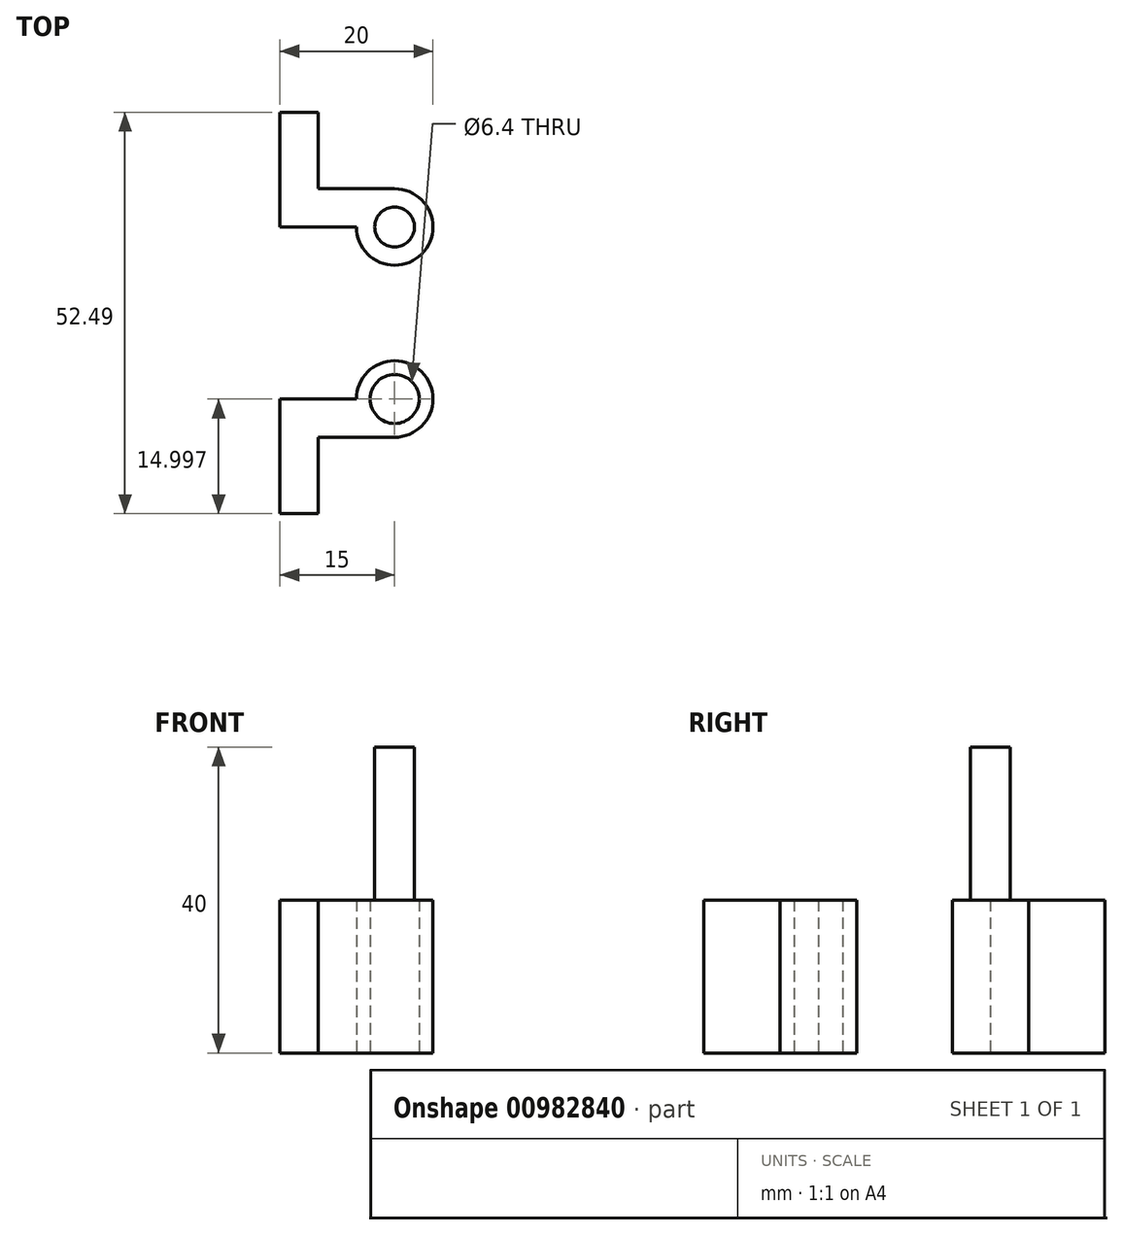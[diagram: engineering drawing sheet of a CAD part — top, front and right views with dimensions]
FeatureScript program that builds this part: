
annotation { "Feature Type Name" : "Feature", "Feature Type Description" : "" }
export const myFeature = defineFeature(function(context is Context, id is Id, definition is map)
    precondition{}
    {
        {
            var Q0;
            Q0=qCreatedBy(makeId("Top.planeOp"),FACE);
            var sketch = newSketch(context, id + "F0", { "sketchPlane" : qUnion([Q0])});
            skCircle(sketch, "E0", {"center": v(0, 0) * mm, "radius": 2.6 * mm});
            skLineSegment(sketch, "E1", {"start": v(-15, 5) * mm, "end": v(-15, 0) * mm});
            skLineSegment(sketch, "E2", {"start": v(-15, 0) * mm, "end": v(-5, 0) * mm});
            skCircle(sketch, "E3", {"center": v(0, -22.5) * mm, "radius": 3.2 * mm});
            skArc(sketch, "E4", {"start": v(0, -27.5) * mm, "mid": v(3.54, -18.96) * mm, "end": v(-5, -22.5) * mm});
            skLineSegment(sketch, "E5", {"start": v(-15, -22.5) * mm, "end": v(-15, -27.5) * mm});
            skLineSegment(sketch, "E6", {"start": v(-15, 5) * mm, "end": v(-15, 15) * mm});
            skLineSegment(sketch, "E7", {"start": v(-15, 15) * mm, "end": v(-10, 15) * mm});
            skLineSegment(sketch, "E8", {"start": v(-10, 15) * mm, "end": v(-10, 5) * mm});
            skLineSegment(sketch, "E9", {"start": v(-10, 5) * mm, "end": v(0, 5) * mm});
            skLineSegment(sketch, "E10", {"start": v(-15, -22.5) * mm, "end": v(-5, -22.5) * mm});
            skLineSegment(sketch, "E11", {"start": v(-15, -27.5) * mm, "end": v(-15, -37.5) * mm});
            skLineSegment(sketch, "E12", {"start": v(-15, -37.5) * mm, "end": v(-10, -37.5) * mm});
            skLineSegment(sketch, "E13", {"start": v(-10, -37.5) * mm, "end": v(-10, -27.5) * mm});
            skLineSegment(sketch, "E14", {"start": v(-10, -27.5) * mm, "end": v(0, -27.5) * mm});
            skArc(sketch, "E15", {"start": v(-5, 0) * mm, "mid": v(3.54, -3.54) * mm, "end": v(0, 5) * mm});
            skLineSegment(sketch, "E16", {"start": v(0, -2.6) * mm, "end": v(0, -5) * mm, "construction": true});
            skLineSegment(sketch, "E17", {"start": v(0, -27.5) * mm, "end": v(0, -25.7) * mm, "construction": true});
            skSolve(sketch);
        }
        {
            var Q0;
            Q0=makeQuery(id+"F0.imprint","IMPRINT",FACE,{"disambiguationData":[TD([[makeQuery(id+"F0.imprint","IMPRINT",EDGE,{"derivedFrom":sQuery(id+"F0.wireOp",EDGE,"E0")}),-1.0]])]});
            var Q1;
            Q1=makeQuery(id+"F0.imprint","IMPRINT",FACE,{"disambiguationData":[TD([[makeQuery(id+"F0.imprint","IMPRINT",EDGE,{"derivedFrom":sQuery(id+"F0.wireOp",EDGE,"E3")}),-1.0]])]});
            extrude(context, id + "F1", {"entities" : qUnion([Q0, Q1]), "depth" : 20 * mm, "offsetDistance" : 25 * mm});
        }
        {
            var Q0;
            Q0=makeQuery(id+"F0.imprint","IMPRINT",FACE,{"disambiguationData":[TD([[makeQuery(id+"F0.imprint","IMPRINT",EDGE,{"derivedFrom":sQuery(id+"F0.wireOp",EDGE,"E0")}),1.0]])]});
            extrude(context, id + "F2", {"entities" : qUnion([Q0]), "operationType" : NewBodyOperationType.ADD, "depth" : 40 * mm, "offsetDistance" : 25 * mm});
        }
    });
